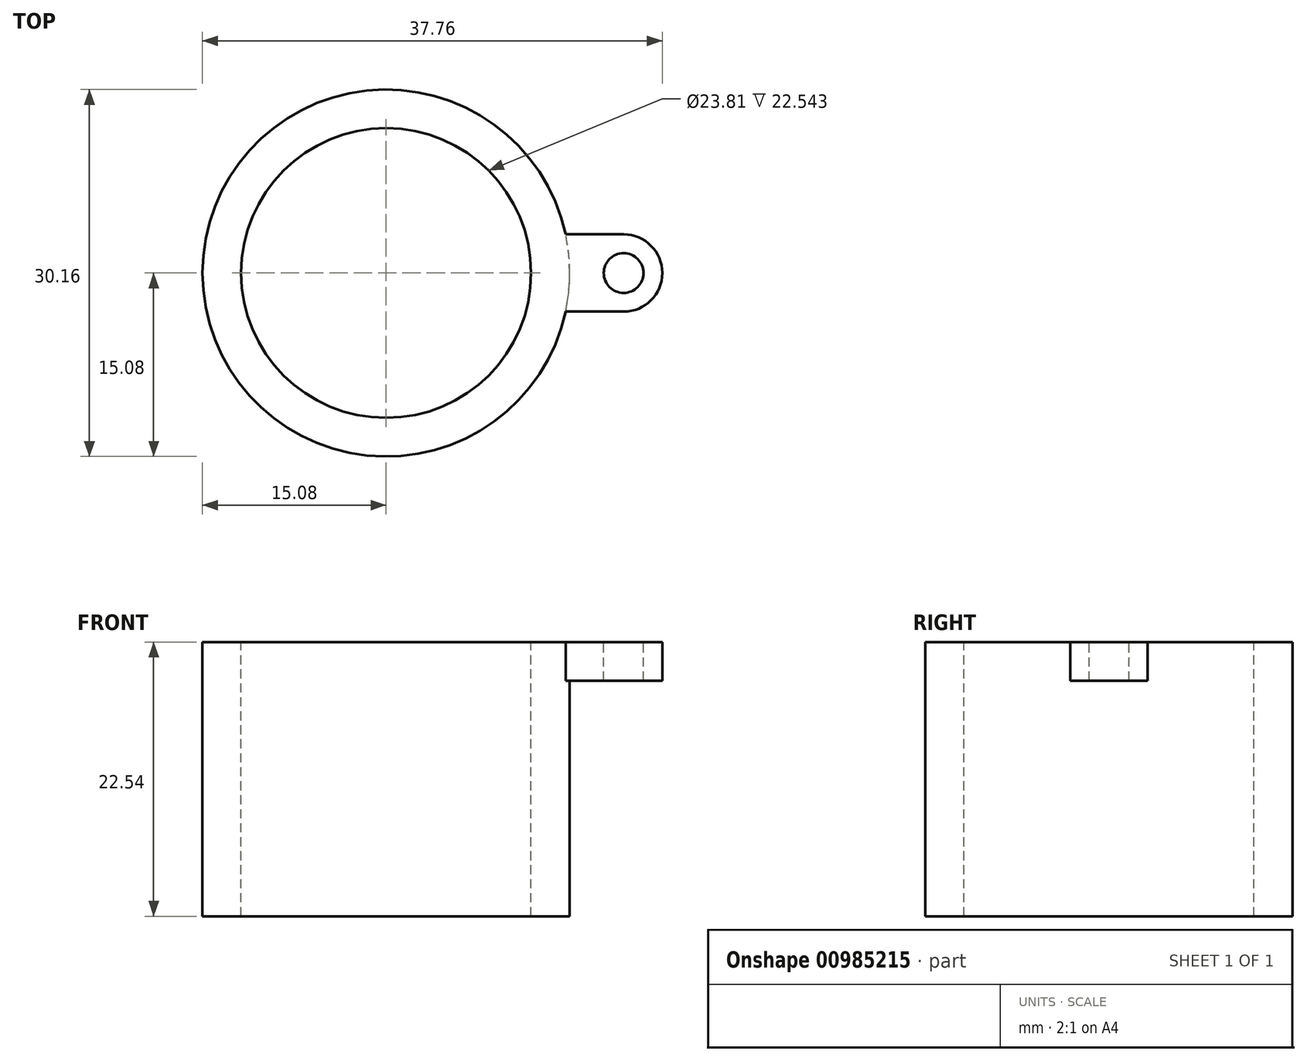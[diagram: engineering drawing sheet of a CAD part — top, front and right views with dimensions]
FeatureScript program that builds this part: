
annotation { "Feature Type Name" : "Feature", "Feature Type Description" : "" }
export const myFeature = defineFeature(function(context is Context, id is Id, definition is map)
    precondition{}
    {
        {
            var Q0;
            Q0=qCreatedBy(makeId("Top.planeOp"),FACE);
            var sketch = newSketch(context, id + "F0", { "sketchPlane" : qUnion([Q0])});
            skCircle(sketch, "E0", {"center": v(0, 0) * mm, "radius": 11.9 * mm});
            skCircle(sketch, "E1", {"center": v(0, 0) * mm, "radius": 15.08 * mm});
            skSolve(sketch);
        }
        {
            var Q0;
            Q0 = qSketchRegion(id + "F0", true);
            extrude(context, id + "F1", {"entities" : qUnion([Q0]), "oppositeDirection" : true, "depth" : 22.54 * mm, "offsetDistance" : 25.4 * mm});
        }
        {
            var Q0;
            Q0=qCreatedBy(makeId("Top.planeOp"),FACE);
            var sketch = newSketch(context, id + "F2", { "sketchPlane" : qUnion([Q0])});
            skLineSegment(sketch, "E2.bottom", {"start": v(14.74, 3.18) * mm, "end": v(19.5, 3.18) * mm});
            skLineSegment(sketch, "E2.top", {"start": v(14.74, -3.18) * mm, "end": v(19.5, -3.18) * mm});
            skLineSegment(sketch, "E2.left", {"start": v(14.74, 3.18) * mm, "end": v(14.74, -3.18) * mm});
            skCircle(sketch, "E3", {"center": v(19.5, 0) * mm, "radius": 1.63 * mm});
            skArc(sketch, "E4", {"start": v(19.5, -3.18) * mm, "mid": v(22.68, 0) * mm, "end": v(19.5, 3.18) * mm});
            skSolve(sketch);
        }
        {
            var Q0;
            Q0 = qSketchRegion(id + "F2", true);
            extrude(context, id + "F3", {"entities" : qUnion([Q0]), "operationType" : NewBodyOperationType.ADD, "oppositeDirection" : true, "depth" : 3.17 * mm, "offsetDistance" : 25.4 * mm});
        }
    });
